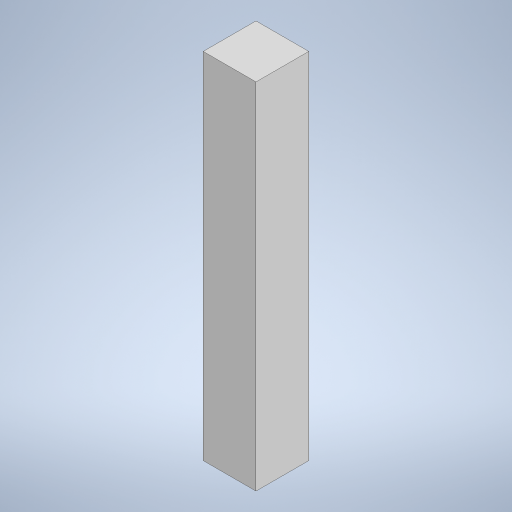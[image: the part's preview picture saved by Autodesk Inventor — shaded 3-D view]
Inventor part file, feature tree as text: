
AUTODESK INVENTOR PART (.ipt)
format: ipt  version: 2024 (Build 280153000, 153)  size: 217,088 bytes
history: native  units: mm
features: extrude x1, sketch x1
ambient origin geometry x8: Origin, YZ Plane, XZ Plane, XY Plane, X Axis, Y Axis, Z Axis, Center Point
bodies: Solido1 (feature_tree)
feature tree (2):
  extrude  "Estrusione1"  Depth=100.0mm
  sketch  "Schizzo1"
